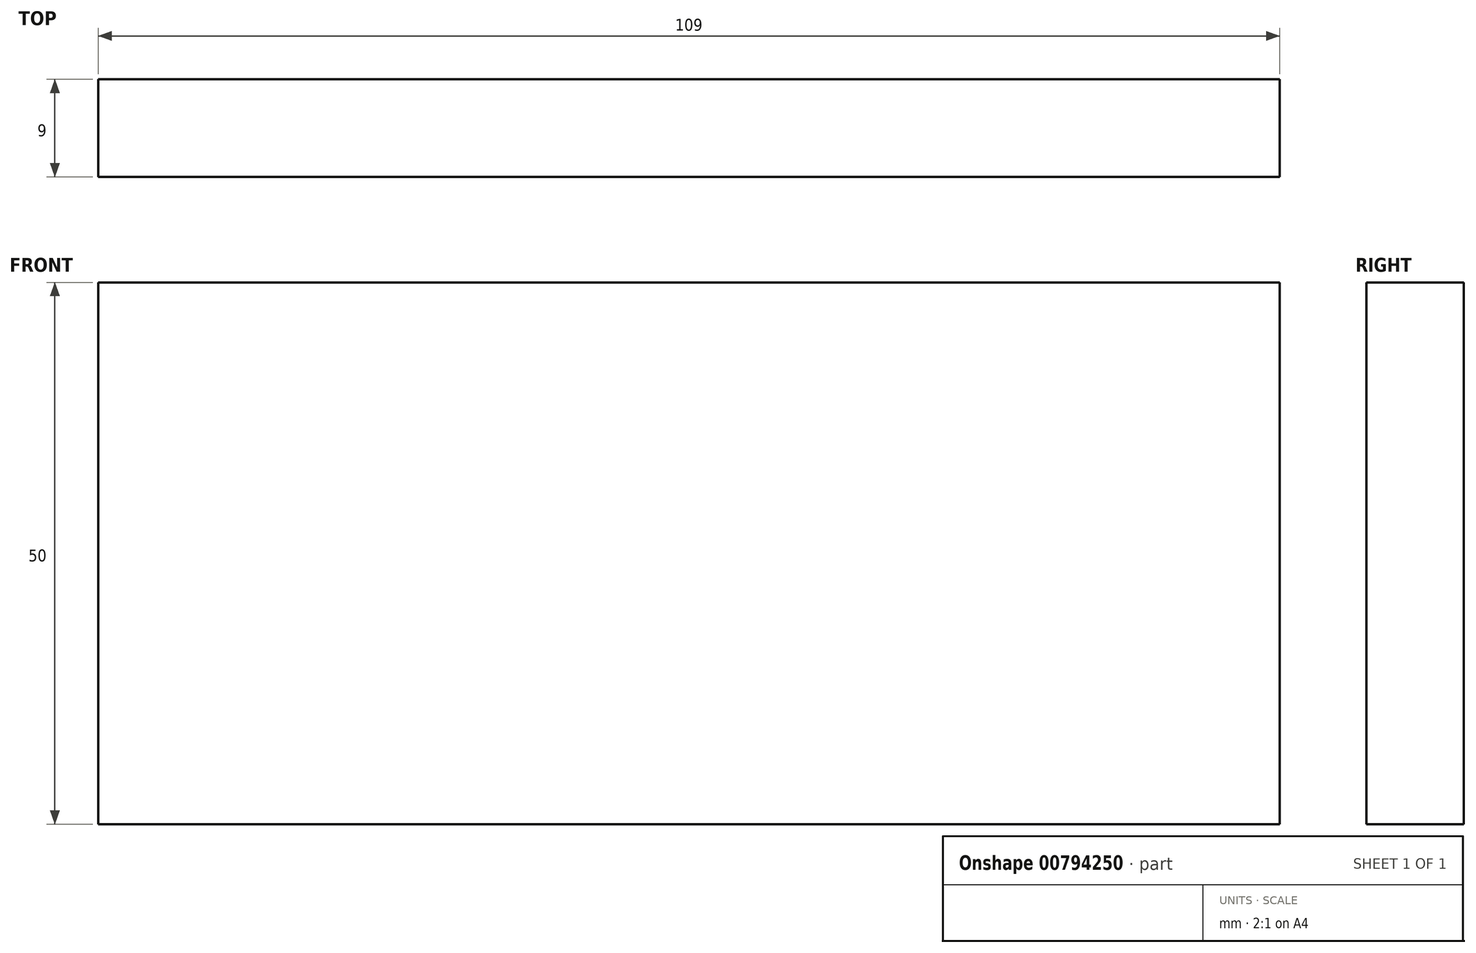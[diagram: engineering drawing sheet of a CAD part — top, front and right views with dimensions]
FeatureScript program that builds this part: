
annotation { "Feature Type Name" : "Feature", "Feature Type Description" : "" }
export const myFeature = defineFeature(function(context is Context, id is Id, definition is map)
    precondition{}
    {
        {
            var Q0;
            Q0=qCreatedBy(makeId("Top.planeOp"),FACE);
            var sketch = newSketch(context, id + "F0", { "sketchPlane" : qUnion([Q0])});
            skLineSegment(sketch, "E0.bottom", {"start": v(54.5, 4.5) * mm, "end": v(-54.5, 4.5) * mm});
            skLineSegment(sketch, "E0.top", {"start": v(54.5, -4.5) * mm, "end": v(-54.5, -4.5) * mm});
            skLineSegment(sketch, "E0.left", {"start": v(54.5, 4.5) * mm, "end": v(54.5, -4.5) * mm});
            skLineSegment(sketch, "E0.right", {"start": v(-54.5, 4.5) * mm, "end": v(-54.5, -4.5) * mm});
            skPoint(sketch, "E0.middle", {"position": v(0, 0) * mm});
            skSolve(sketch);
        }
        {
            var Q0;
            Q0=makeQuery(id+"F0.imprint","IMPRINT",FACE,{"disambiguationData":[TD([[makeQuery(id+"F0.imprint","IMPRINT",EDGE,{"derivedFrom":sQuery(id+"F0.wireOp",EDGE,"E0.bottom")}),1.0]])]});
            extrude(context, id + "F1", {"entities" : qUnion([Q0]), "depth" : 50 * mm, "offsetDistance" : 25 * mm});
        }
    });
